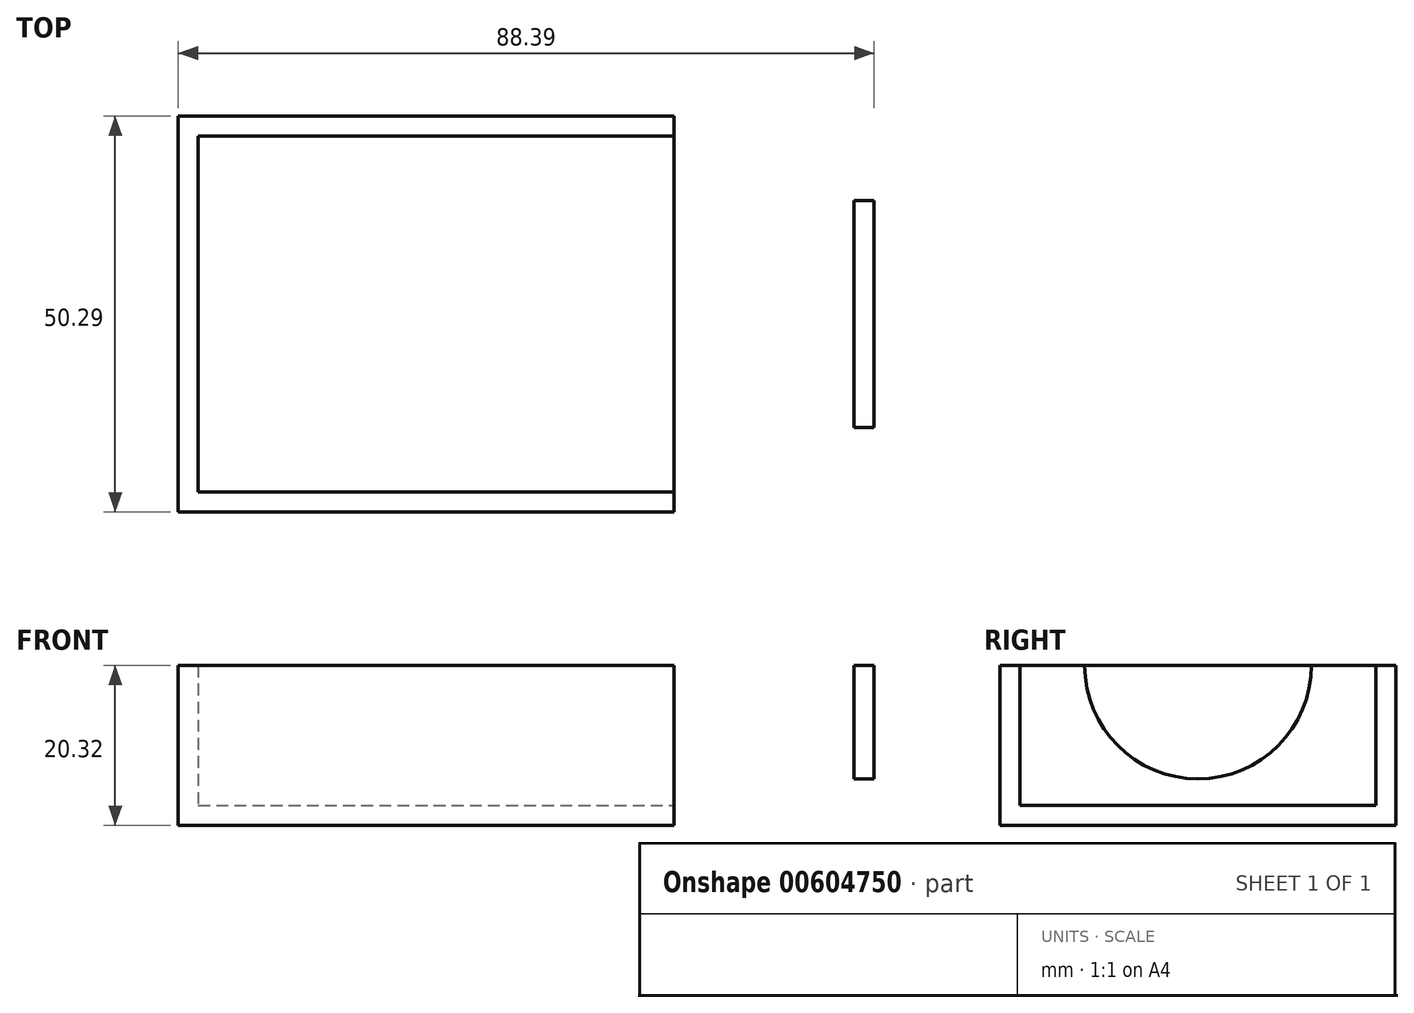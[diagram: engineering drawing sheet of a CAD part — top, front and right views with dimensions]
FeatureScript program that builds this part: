
annotation { "Feature Type Name" : "Feature", "Feature Type Description" : "" }
export const myFeature = defineFeature(function(context is Context, id is Id, definition is map)
    precondition{}
    {
        {
            var Q0;
            Q0=qCreatedBy(makeId("Top.planeOp"),FACE);
            var sketch = newSketch(context, id + "F0", { "sketchPlane" : qUnion([Q0])});
            skLineSegment(sketch, "E0.bottom", {"start": v(0, 0) * mm, "end": v(88.4, 0) * mm});
            skLineSegment(sketch, "E0.top", {"start": v(0, 50.3) * mm, "end": v(88.4, 50.3) * mm});
            skLineSegment(sketch, "E0.left", {"start": v(0, 0) * mm, "end": v(0, 50.3) * mm});
            skLineSegment(sketch, "E0.right", {"start": v(88.4, 0) * mm, "end": v(88.4, 50.3) * mm});
            skSolve(sketch);
        }
        {
            var Q0;
            Q0=makeQuery(id+"F0.imprint","IMPRINT",FACE,{"disambiguationData":[TD([[makeQuery(id+"F0.imprint","IMPRINT",EDGE,{"derivedFrom":sQuery(id+"F0.wireOp",EDGE,"E0.bottom")}),1.0]])]});
            extrude(context, id + "F1", {"entities" : qUnion([Q0]), "depth" : 20.32 * mm, "offsetDistance" : 25.4 * mm});
        }
        {
            var Q0;
            Q0=makeQuery(id+"F1.opExtrude","CAP_FACE",FACE,{"disambiguationData":[OSD([sQuery(id+"F0.wireOp",EDGE,"E0.bottom"),sQuery(id+"F0.wireOp",EDGE,"E0.top"),sQuery(id+"F0.wireOp",EDGE,"E0.left"),sQuery(id+"F0.wireOp",EDGE,"E0.right")])],"isStart":false});
            shell(context, id + "F2", {"entities" : qUnion([Q0]), "thickness" : 2.54 * mm});
        }
        {
            var Q0;
            Q0=makeQuery(id+"F1.opExtrude","SWEPT_FACE",FACE,{"disambiguationData":[OSD([sQuery(id+"F0.wireOp",EDGE,"E0.right")])]});
            var sketch = newSketch(context, id + "F3", { "sketchPlane" : qUnion([Q0])});
            skArc(sketch, "E1", {"start": v(39.55, 20.32) * mm, "mid": v(25.15, 5.92) * mm, "end": v(10.74, 20.32) * mm});
            skSolve(sketch);
        }
        {
            var Q0;
            {var subQ0=sQuery(id+"F3.wireOp",EDGE,"E1");Q0=makeQuery(id+"F3.imprint","IMPRINT",FACE,{"disambiguationData":[TD([[makeQuery(id+"F3.imprint","IMPRINT",EDGE,{"derivedFrom":subQ0}),-1.0]])]});}
            extrude(context, id + "F4", {"entities" : qUnion([Q0]), "operationType" : NewBodyOperationType.REMOVE, "oppositeDirection" : true, "depth" : 25.4 * mm, "offsetDistance" : 25.4 * mm});
        }
    });
